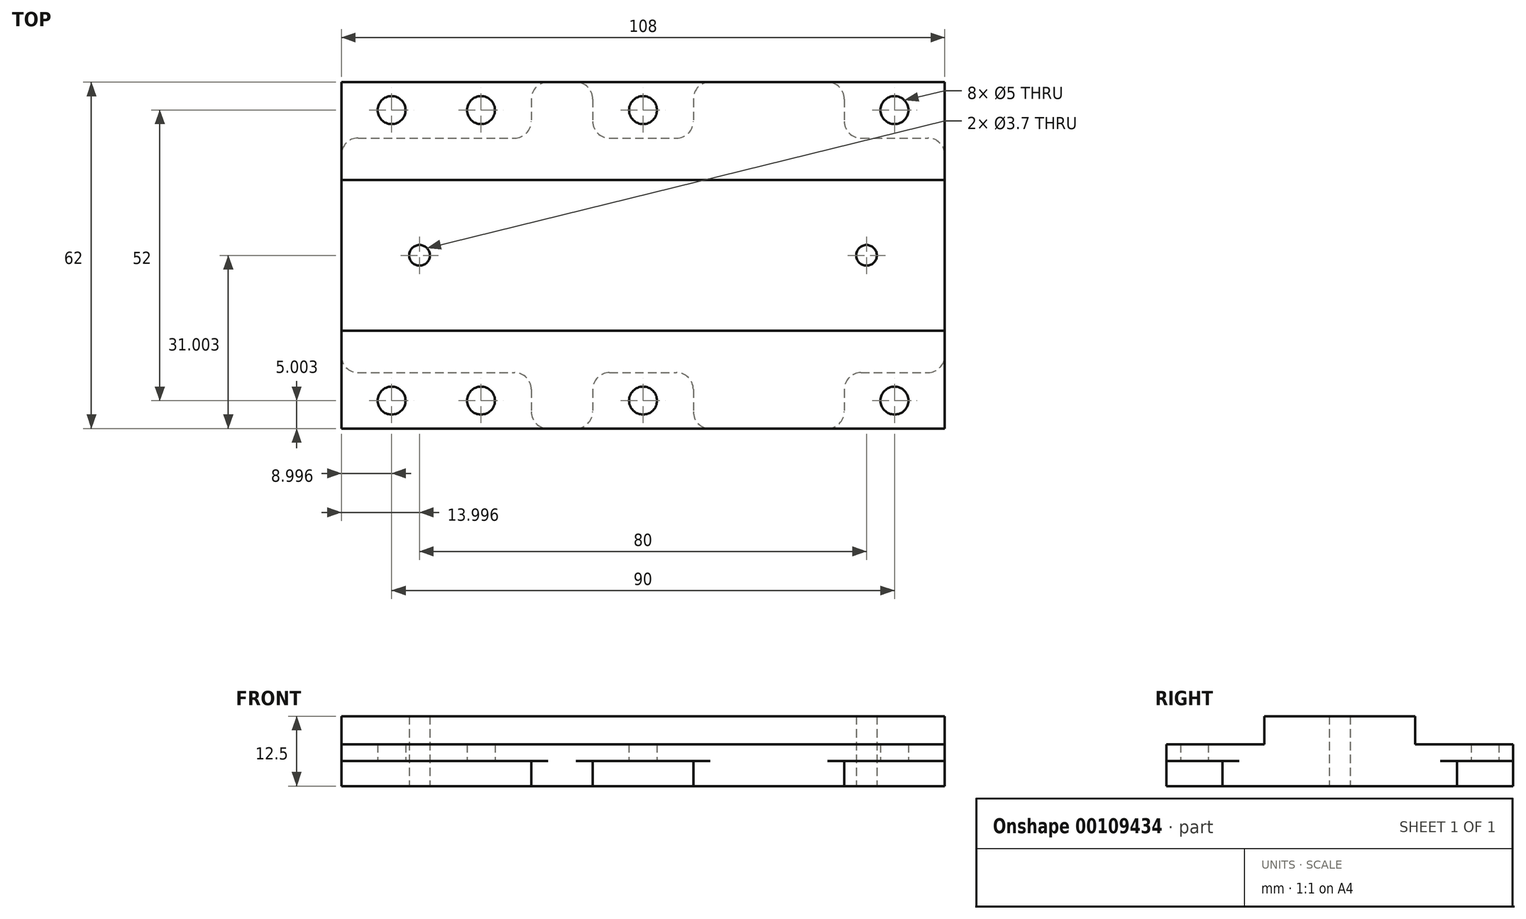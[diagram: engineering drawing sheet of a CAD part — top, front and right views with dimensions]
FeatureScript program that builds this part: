
annotation { "Feature Type Name" : "Feature", "Feature Type Description" : "" }
export const myFeature = defineFeature(function(context is Context, id is Id, definition is map)
    precondition{}
    {
        {
            var Q0;
            Q0=qCreatedBy(makeId("Top.planeOp"),FACE);
            var sketch = newSketch(context, id + "F0", { "sketchPlane" : qUnion([Q0])});
            skLineSegment(sketch, "E0.bottom", {"start": v(-30.67, 42.04) * mm, "end": v(-19.67, 42.04) * mm});
            skLineSegment(sketch, "E0.top", {"start": v(-30.67, -19.96) * mm, "end": v(-19.67, -19.96) * mm});
            skLineSegment(sketch, "E0.left", {"start": v(-64.67, 32.04) * mm, "end": v(-64.67, -9.96) * mm});
            skLineSegment(sketch, "E0.right", {"start": v(43.33, 32.04) * mm, "end": v(43.33, -9.96) * mm});
            skLineSegment(sketch, "E1.bottom", {"start": v(-64.67, 32.04) * mm, "end": v(43.33, 32.04) * mm});
            skLineSegment(sketch, "E1.top", {"start": v(-64.67, -9.96) * mm, "end": v(43.33, -9.96) * mm});
            skLineSegment(sketch, "E2", {"start": v(-30.67, 42.04) * mm, "end": v(-30.67, -19.96) * mm});
            skLineSegment(sketch, "E3", {"start": v(25.33, 42.04) * mm, "end": v(25.33, -19.96) * mm});
            skLineSegment(sketch, "E4", {"start": v(-19.67, 42.04) * mm, "end": v(-19.67, -19.96) * mm});
            skLineSegment(sketch, "E5", {"start": v(-1.67, 42.04) * mm, "end": v(-1.67, -19.96) * mm});
            skLineSegment(sketch, "E6.trimOffspring", {"start": v(-1.67, -19.96) * mm, "end": v(25.33, -19.96) * mm});
            skLineSegment(sketch, "E7.trimOffspring", {"start": v(-1.67, 42.04) * mm, "end": v(25.33, 42.04) * mm});
            skSolve(sketch);
        }
        {
            var Q0;
            Q0 = qSketchRegion(id + "F0", true);
            extrude(context, id + "F1", {"entities" : qUnion([Q0]), "depth" : 4.5 * mm});
        }
        {
            var Q0;
            Q0=makeQuery(id+"F1.opExtrude","SWEPT_EDGE",EDGE,{"disambiguationData":[OSD([sQuery(id+"F0.wireOp",EDGE,"E1.bottom"),sQuery(id+"F0.wireOp",EDGE,"E0.left")])]});
            var Q1;
            Q1=makeQuery(id+"F1.opExtrude","SWEPT_EDGE",EDGE,{"disambiguationData":[OSD([sQuery(id+"F0.wireOp",EDGE,"E0.bottom"),sQuery(id+"F0.wireOp",EDGE,"E2")])]});
            var Q2;
            Q2=makeQuery(id+"F1.opExtrude","SWEPT_EDGE",EDGE,{"disambiguationData":[OSD([sQuery(id+"F0.wireOp",EDGE,"E0.bottom"),sQuery(id+"F0.wireOp",EDGE,"E4")])]});
            var Q3;
            Q3=makeQuery(id+"F1.opExtrude","SWEPT_EDGE",EDGE,{"disambiguationData":[OSD([sQuery(id+"F0.wireOp",EDGE,"E5"),sQuery(id+"F0.wireOp",EDGE,"E7.trimOffspring")])]});
            var Q4;
            Q4=makeQuery(id+"F1.opExtrude","SWEPT_EDGE",EDGE,{"disambiguationData":[OSD([sQuery(id+"F0.wireOp",EDGE,"E3"),sQuery(id+"F0.wireOp",EDGE,"E7.trimOffspring")])]});
            var Q5;
            Q5=makeQuery(id+"F1.opExtrude","SWEPT_EDGE",EDGE,{"disambiguationData":[OSD([sQuery(id+"F0.wireOp",EDGE,"E1.bottom"),sQuery(id+"F0.wireOp",EDGE,"E5")])]});
            var Q6;
            Q6=makeQuery(id+"F1.opExtrude","SWEPT_EDGE",EDGE,{"disambiguationData":[OSD([sQuery(id+"F0.wireOp",EDGE,"E1.bottom"),sQuery(id+"F0.wireOp",EDGE,"E4")])]});
            var Q7;
            Q7=makeQuery(id+"F1.opExtrude","SWEPT_EDGE",EDGE,{"disambiguationData":[OSD([sQuery(id+"F0.wireOp",EDGE,"E1.bottom"),sQuery(id+"F0.wireOp",EDGE,"E3")])]});
            var Q8;
            Q8=makeQuery(id+"F1.opExtrude","SWEPT_EDGE",EDGE,{"disambiguationData":[OSD([sQuery(id+"F0.wireOp",EDGE,"E1.bottom"),sQuery(id+"F0.wireOp",EDGE,"E0.right")])]});
            var Q9;
            Q9=makeQuery(id+"F1.opExtrude","SWEPT_EDGE",EDGE,{"disambiguationData":[OSD([sQuery(id+"F0.wireOp",EDGE,"E1.top"),sQuery(id+"F0.wireOp",EDGE,"E0.right")])]});
            var Q10;
            Q10=makeQuery(id+"F1.opExtrude","SWEPT_EDGE",EDGE,{"disambiguationData":[OSD([sQuery(id+"F0.wireOp",EDGE,"E1.top"),sQuery(id+"F0.wireOp",EDGE,"E3")])]});
            var Q11;
            Q11=makeQuery(id+"F1.opExtrude","SWEPT_EDGE",EDGE,{"disambiguationData":[OSD([sQuery(id+"F0.wireOp",EDGE,"E3"),sQuery(id+"F0.wireOp",EDGE,"E6.trimOffspring")])]});
            var Q12;
            Q12=makeQuery(id+"F1.opExtrude","SWEPT_EDGE",EDGE,{"disambiguationData":[OSD([sQuery(id+"F0.wireOp",EDGE,"E5"),sQuery(id+"F0.wireOp",EDGE,"E6.trimOffspring")])]});
            var Q13;
            Q13=makeQuery(id+"F1.opExtrude","SWEPT_EDGE",EDGE,{"disambiguationData":[OSD([sQuery(id+"F0.wireOp",EDGE,"E1.top"),sQuery(id+"F0.wireOp",EDGE,"E5")])]});
            var Q14;
            Q14=makeQuery(id+"F1.opExtrude","SWEPT_EDGE",EDGE,{"disambiguationData":[OSD([sQuery(id+"F0.wireOp",EDGE,"E1.top"),sQuery(id+"F0.wireOp",EDGE,"E4")])]});
            var Q15;
            Q15=makeQuery(id+"F1.opExtrude","SWEPT_EDGE",EDGE,{"disambiguationData":[OSD([sQuery(id+"F0.wireOp",EDGE,"E0.top"),sQuery(id+"F0.wireOp",EDGE,"E4")])]});
            var Q16;
            Q16=makeQuery(id+"F1.opExtrude","SWEPT_EDGE",EDGE,{"disambiguationData":[OSD([sQuery(id+"F0.wireOp",EDGE,"E0.top"),sQuery(id+"F0.wireOp",EDGE,"E2")])]});
            var Q17;
            Q17=makeQuery(id+"F1.opExtrude","SWEPT_EDGE",EDGE,{"disambiguationData":[OSD([sQuery(id+"F0.wireOp",EDGE,"E1.top"),sQuery(id+"F0.wireOp",EDGE,"E2")])]});
            var Q18;
            Q18=makeQuery(id+"F1.opExtrude","SWEPT_EDGE",EDGE,{"disambiguationData":[OSD([sQuery(id+"F0.wireOp",EDGE,"E1.top"),sQuery(id+"F0.wireOp",EDGE,"E0.left")])]});
            var Q19;
            Q19=makeQuery(id+"F1.opExtrude","SWEPT_EDGE",EDGE,{"disambiguationData":[OSD([sQuery(id+"F0.wireOp",EDGE,"E1.bottom"),sQuery(id+"F0.wireOp",EDGE,"E2")])]});
            fillet(context, id + "F2", {"entities" : qUnion([Q0, Q1, Q2, Q3, Q4, Q5, Q6, Q7, Q8, Q9, Q10, Q11, Q12, Q13, Q14, Q15, Q16, Q17, Q18, Q19]), "radius" : 3 * mm, "tangentPropagation" : true, "allowEdgeOverflow" : false});
        }
        {
            var Q0;
            Q0=makeQuery(id+"F1.opExtrude","CAP_FACE",FACE,{"disambiguationData":[OSD([sQuery(id+"F0.wireOp",EDGE,"E0.bottom"),sQuery(id+"F0.wireOp",EDGE,"E0.top"),sQuery(id+"F0.wireOp",EDGE,"E1.bottom"),sQuery(id+"F0.wireOp",EDGE,"E1.top"),sQuery(id+"F0.wireOp",EDGE,"E0.left"),sQuery(id+"F0.wireOp",EDGE,"E0.right"),sQuery(id+"F0.wireOp",EDGE,"E2"),sQuery(id+"F0.wireOp",EDGE,"E3"),sQuery(id+"F0.wireOp",EDGE,"E4"),sQuery(id+"F0.wireOp",EDGE,"E5"),sQuery(id+"F0.wireOp",EDGE,"E6.trimOffspring"),sQuery(id+"F0.wireOp",EDGE,"E7.trimOffspring")])],"isStart":false});
            var sketch = newSketch(context, id + "F3", { "sketchPlane" : qUnion([Q0])});
            skLineSegment(sketch, "E8.bottom", {"start": v(-64.67, 42.04) * mm, "end": v(43.33, 42.04) * mm});
            skLineSegment(sketch, "E8.top", {"start": v(-64.67, -19.96) * mm, "end": v(43.33, -19.96) * mm});
            skLineSegment(sketch, "E8.left", {"start": v(-64.67, 42.04) * mm, "end": v(-64.67, -19.96) * mm});
            skLineSegment(sketch, "E8.right", {"start": v(43.33, 42.04) * mm, "end": v(43.33, -19.96) * mm});
            skLineSegment(sketch, "E9", {"start": v(-19.67, 37.04) * mm, "end": v(-1.67, 37.04) * mm});
            skLineSegment(sketch, "E10", {"start": v(25.33, 37.04) * mm, "end": v(43.33, 37.04) * mm});
            skLineSegment(sketch, "E11", {"start": v(-30.67, 37.04) * mm, "end": v(-64.67, 37.04) * mm});
            skLineSegment(sketch, "E12", {"start": v(-30.67, -14.96) * mm, "end": v(-64.67, -14.96) * mm});
            skLineSegment(sketch, "E13", {"start": v(-19.67, -14.96) * mm, "end": v(-1.67, -14.96) * mm});
            skLineSegment(sketch, "E14", {"start": v(25.33, -14.96) * mm, "end": v(43.33, -14.96) * mm});
            skCircle(sketch, "E15", {"center": v(-10.67, 37.04) * mm, "radius": 2.5 * mm});
            skCircle(sketch, "E16", {"center": v(-10.67, -14.96) * mm, "radius": 2.5 * mm});
            skCircle(sketch, "E17", {"center": v(34.33, 37.04) * mm, "radius": 2.5 * mm});
            skCircle(sketch, "E18", {"center": v(34.33, -14.96) * mm, "radius": 2.5 * mm});
            skCircle(sketch, "E19", {"center": v(-39.67, 37.04) * mm, "radius": 2.5 * mm});
            skCircle(sketch, "E20", {"center": v(-55.67, 37.04) * mm, "radius": 2.5 * mm});
            skCircle(sketch, "E21", {"center": v(-39.67, -14.96) * mm, "radius": 2.5 * mm});
            skCircle(sketch, "E22", {"center": v(-55.67, -14.96) * mm, "radius": 2.5 * mm});
            skSolve(sketch);
        }
        {
            var Q0;
            Q0 = qSketchRegion(id + "F3", true);
            extrude(context, id + "F4", {"entities" : qUnion([Q0]), "operationType" : NewBodyOperationType.ADD, "depth" : 3 * mm});
        }
        {
            var Q0;
            Q0=makeQuery(id+"F4.opExtrude","CAP_FACE",FACE,{"disambiguationData":[OSD([sQuery(id+"F3.wireOp",EDGE,"E8.bottom"),sQuery(id+"F3.wireOp",EDGE,"E8.top"),sQuery(id+"F3.wireOp",EDGE,"E8.left"),sQuery(id+"F3.wireOp",EDGE,"E8.right"),sQuery(id+"F3.wireOp",EDGE,"E15"),sQuery(id+"F3.wireOp",EDGE,"E16"),sQuery(id+"F3.wireOp",EDGE,"E17"),sQuery(id+"F3.wireOp",EDGE,"E18"),sQuery(id+"F3.wireOp",EDGE,"E19"),sQuery(id+"F3.wireOp",EDGE,"E20"),sQuery(id+"F3.wireOp",EDGE,"E21"),sQuery(id+"F3.wireOp",EDGE,"E22")])],"isStart":false});
            var sketch = newSketch(context, id + "F5", { "sketchPlane" : qUnion([Q0])});
            skLineSegment(sketch, "E23.bottom", {"start": v(-64.67, 24.54) * mm, "end": v(43.33, 24.54) * mm});
            skLineSegment(sketch, "E23.top", {"start": v(-64.67, -2.46) * mm, "end": v(43.33, -2.46) * mm});
            skLineSegment(sketch, "E23.left", {"start": v(-64.67, 24.54) * mm, "end": v(-64.67, -2.46) * mm});
            skLineSegment(sketch, "E23.right", {"start": v(43.33, 24.54) * mm, "end": v(43.33, -2.46) * mm});
            skLineSegment(sketch, "E24", {"start": v(-64.67, 11.04) * mm, "end": v(43.33, 11.04) * mm});
            skLineSegment(sketch, "E25", {"start": v(-50.67, 24.54) * mm, "end": v(-50.67, -2.46) * mm});
            skLineSegment(sketch, "E26", {"start": v(29.33, 24.54) * mm, "end": v(29.33, -2.46) * mm});
            skCircle(sketch, "E27", {"center": v(-50.67, 11.04) * mm, "radius": 1.85 * mm});
            skCircle(sketch, "E28", {"center": v(29.33, 11.04) * mm, "radius": 1.85 * mm});
            skSolve(sketch);
        }
        {
            var Q0;
            Q0 = qSketchRegion(id + "F5", true);
            extrude(context, id + "F6", {"entities" : qUnion([Q0]), "operationType" : NewBodyOperationType.ADD, "depth" : 5 * mm});
        }
        {
            var Q0;
            Q0=makeQuery(id+"F6.boolean.opBoolean","SPLIT",FACE,{"disambiguationData":[TD([makeQuery(id+"F6.opExtrude","SWEPT_FACE",FACE,{"disambiguationData":[OSD([sQuery(id+"F5.wireOp",EDGE,"E27")])]})])],"derivedFrom":makeQuery(id+"F4.opExtrude","CAP_FACE",FACE,{"disambiguationData":[OSD([sQuery(id+"F3.wireOp",EDGE,"E8.bottom"),sQuery(id+"F3.wireOp",EDGE,"E8.top"),sQuery(id+"F3.wireOp",EDGE,"E8.left"),sQuery(id+"F3.wireOp",EDGE,"E8.right"),sQuery(id+"F3.wireOp",EDGE,"E15"),sQuery(id+"F3.wireOp",EDGE,"E16"),sQuery(id+"F3.wireOp",EDGE,"E17"),sQuery(id+"F3.wireOp",EDGE,"E18"),sQuery(id+"F3.wireOp",EDGE,"E19"),sQuery(id+"F3.wireOp",EDGE,"E20"),sQuery(id+"F3.wireOp",EDGE,"E21"),sQuery(id+"F3.wireOp",EDGE,"E22")])],"isStart":false})});
            extrude(context, id + "F7", {"entities" : qUnion([Q0]), "operationType" : NewBodyOperationType.REMOVE, "oppositeDirection" : true, "depth" : 7.5 * mm});
        }
        {
            var Q0;
            Q0=makeQuery(id+"F6.boolean.opBoolean","SPLIT",FACE,{"disambiguationData":[TD([makeQuery(id+"F6.opExtrude","SWEPT_FACE",FACE,{"disambiguationData":[OSD([sQuery(id+"F5.wireOp",EDGE,"E28")])]})])],"derivedFrom":makeQuery(id+"F4.opExtrude","CAP_FACE",FACE,{"disambiguationData":[OSD([sQuery(id+"F3.wireOp",EDGE,"E8.bottom"),sQuery(id+"F3.wireOp",EDGE,"E8.top"),sQuery(id+"F3.wireOp",EDGE,"E8.left"),sQuery(id+"F3.wireOp",EDGE,"E8.right"),sQuery(id+"F3.wireOp",EDGE,"E15"),sQuery(id+"F3.wireOp",EDGE,"E16"),sQuery(id+"F3.wireOp",EDGE,"E17"),sQuery(id+"F3.wireOp",EDGE,"E18"),sQuery(id+"F3.wireOp",EDGE,"E19"),sQuery(id+"F3.wireOp",EDGE,"E20"),sQuery(id+"F3.wireOp",EDGE,"E21"),sQuery(id+"F3.wireOp",EDGE,"E22")])],"isStart":false})});
            extrude(context, id + "F8", {"entities" : qUnion([Q0]), "operationType" : NewBodyOperationType.REMOVE, "oppositeDirection" : true, "depth" : 7.5 * mm});
        }
    });
